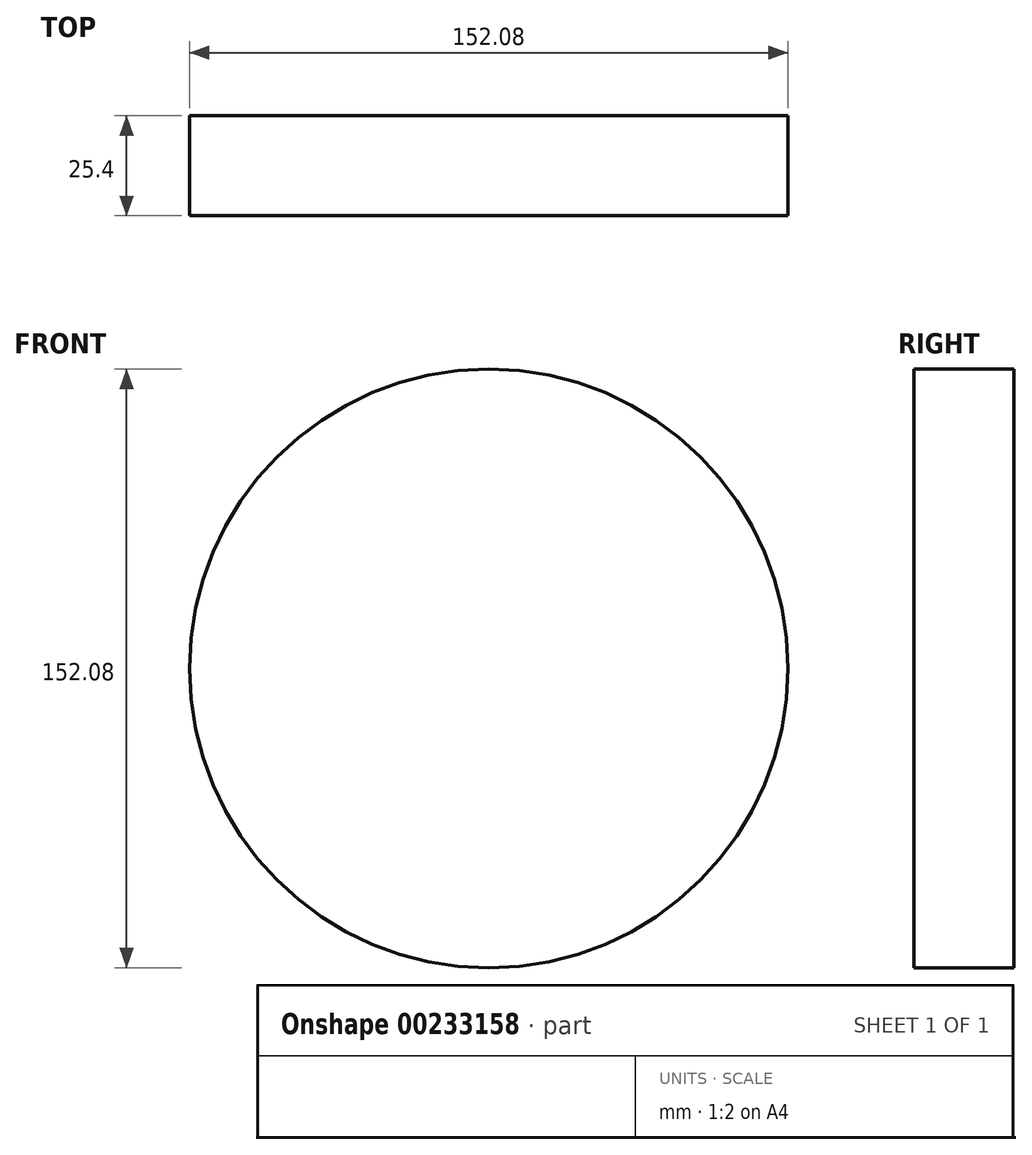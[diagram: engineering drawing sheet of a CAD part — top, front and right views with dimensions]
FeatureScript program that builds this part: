
annotation { "Feature Type Name" : "Feature", "Feature Type Description" : "" }
export const myFeature = defineFeature(function(context is Context, id is Id, definition is map)
    precondition{}
    {
        {
            var Q0;
            Q0=qCreatedBy(makeId("Front.planeOp"),FACE);
            var sketch = newSketch(context, id + "F0", { "sketchPlane" : qUnion([Q0])});
            skCircle(sketch, "E0", {"center": v(0, 0) * mm, "radius": 76.04 * mm});
            skSolve(sketch);
        }
        {
            var Q0;
            Q0=makeQuery(id+"F0.imprint","IMPRINT",FACE,{"disambiguationData":[TD([[makeQuery(id+"F0.imprint","IMPRINT",EDGE,{"derivedFrom":sQuery(id+"F0.wireOp",EDGE,"E0")}),1.0]])]});
            extrude(context, id + "F1", {"entities" : qUnion([Q0]), "depth" : 25.4 * mm});
        }
        {
            var Q0;
            Q0=qCreatedBy(makeId("Front.planeOp"),FACE);
            var sketch = newSketch(context, id + "F2", { "sketchPlane" : qUnion([Q0])});
            skCircle(sketch, "E1", {"center": v(0, 0) * mm, "radius": 61.26 * mm});
            skCircle(sketch, "E2", {"center": v(0, 0) * mm, "radius": 39.18 * mm});
            skCircle(sketch, "E3", {"center": v(0, 0) * mm, "radius": 26.38 * mm});
            skCircle(sketch, "E4", {"center": v(0, 0) * mm, "radius": 16.15 * mm});
            skCircle(sketch, "E5", {"center": v(0, 0) * mm, "radius": 7.72 * mm});
            skSolve(sketch);
        }
        {
            var Q0;
            Q0=sQuery(id+"F2.wireOp",EDGE,"E1");
            extrude(context, id + "F3", {"bodyType" : ToolBodyType.SURFACE, "surfaceEntities" : qUnion([Q0]), "depth" : 25.4 * mm});
        }
        {
            var Q0;
            Q0=makeQuery(id+"F1.opExtrude","CAP_FACE",FACE,{"disambiguationData":[OSD([sQuery(id+"F0.wireOp",EDGE,"E0")])],"isStart":false});
            var sketch = newSketch(context, id + "F4", { "sketchPlane" : qUnion([Q0])});
            skCircle(sketch, "E6.cCircle", {"center": v(0, 0) * mm, "radius": 35.1 * mm, "construction": true});
            skLineSegment(sketch, "E6.0", {"start": v(-60.83, -35.07) * mm, "end": v(0.05, 70.21) * mm});
            skLineSegment(sketch, "E6.1", {"start": v(0.05, 70.21) * mm, "end": v(60.78, -35.15) * mm});
            skLineSegment(sketch, "E6.2", {"start": v(60.78, -35.15) * mm, "end": v(-60.83, -35.07) * mm});
            skPoint(sketch, "E6.0.midPoint", {"position": v(-30.4, 17.57) * mm});
            skArc(sketch, "E7", {"start": v(-35.1, 0) * mm, "mid": v(0, -10.45) * mm, "end": v(35.1, 0) * mm});
            skArc(sketch, "E8", {"start": v(35.1, 0) * mm, "mid": v(0, 10.57) * mm, "end": v(-35.1, 0) * mm});
            skSolve(sketch);
        }
        {
            var Q0;
            Q0=sQuery(id+"F4.wireOp",EDGE,"E6.2");
            var Q1;
            Q1=sQuery(id+"F4.wireOp",EDGE,"E7");
            var Q2;
            Q2=sQuery(id+"F4.wireOp",EDGE,"E8");
            var Q3;
            Q3=sQuery(id+"F4.wireOp",EDGE,"E6.0");
            var Q4;
            Q4=sQuery(id+"F4.wireOp",EDGE,"E6.1");
            extrude(context, id + "F5", {"bodyType" : ToolBodyType.SURFACE, "surfaceEntities" : qUnion([Q0, Q1, Q2, Q3, Q4]), "depth" : 25.4 * mm});
        }
    });
